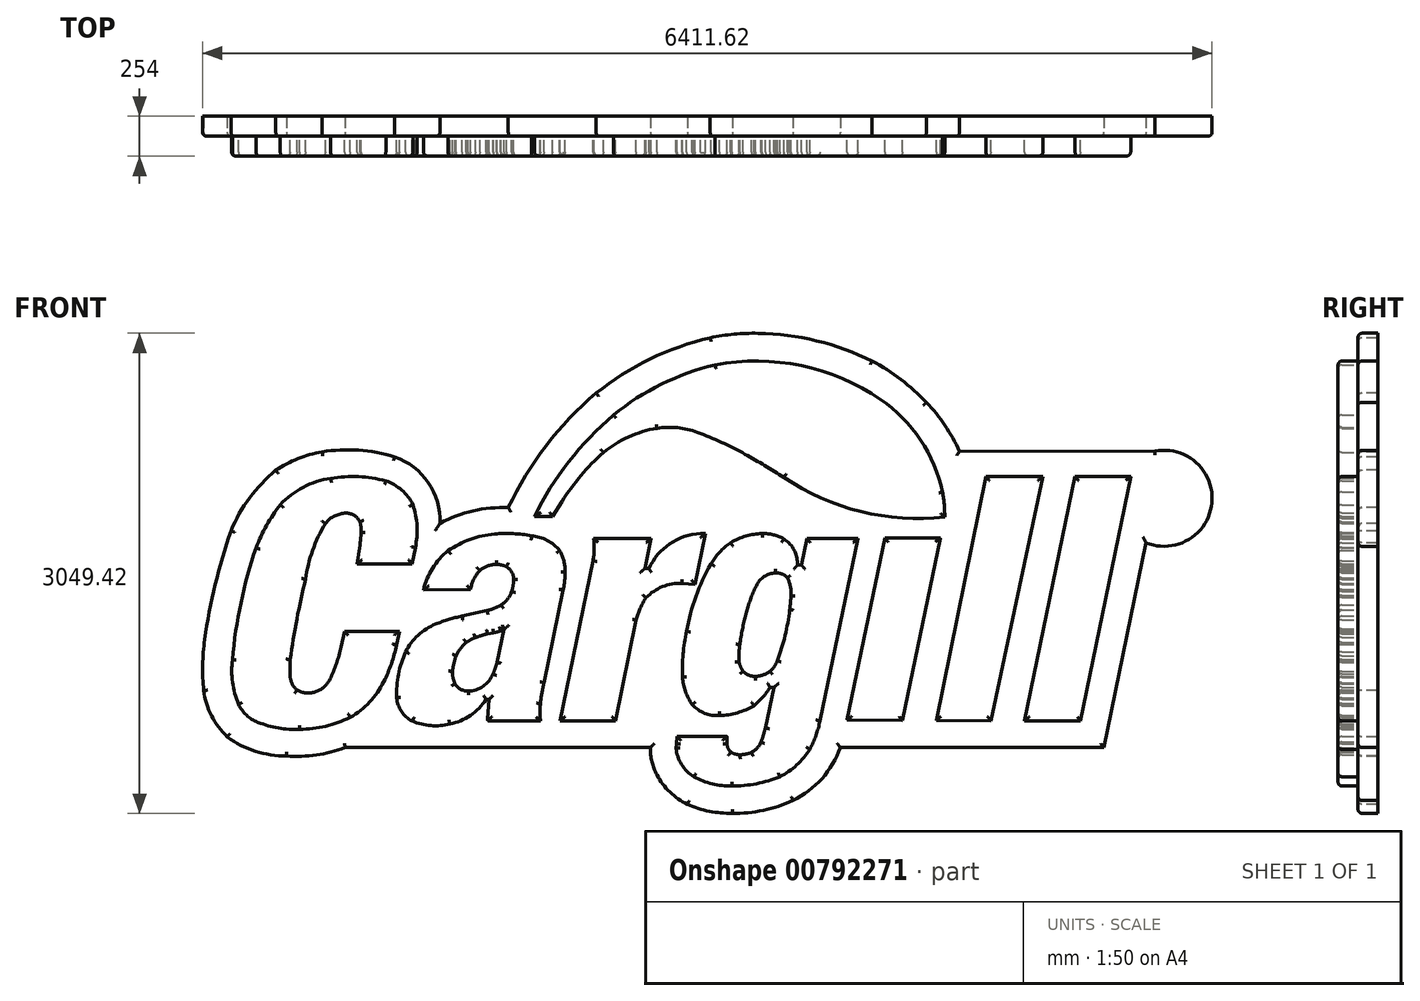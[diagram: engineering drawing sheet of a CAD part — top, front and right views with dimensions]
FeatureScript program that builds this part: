
annotation { "Feature Type Name" : "Feature", "Feature Type Description" : "" }
export const myFeature = defineFeature(function(context is Context, id is Id, definition is map)
    precondition{}
    {
        {
            var Q0;
            Q0=qCreatedBy(makeId("Front.planeOp"),FACE);
            var sketch = newSketch(context, id + "F0", { "sketchPlane" : qUnion([Q0])});
            skArc(sketch, "E0", {"start": v(-1853.74, 164.8) * mm, "mid": v(-1842.63, 301.62) * mm, "end": v(-1868.91, 436.37) * mm});
            skArc(sketch, "E1", {"start": v(-1868.91, 436.37) * mm, "mid": v(-1939.86, 529.44) * mm, "end": v(-2041.08, 588.2) * mm});
            skArc(sketch, "E2", {"start": v(-2041.08, 588.2) * mm, "mid": v(-2215, 614.67) * mm, "end": v(-2390.62, 604.46) * mm});
            skArc(sketch, "E3", {"start": v(-2390.62, 604.46) * mm, "mid": v(-2565.27, 547.67) * mm, "end": v(-2711.35, 436.37) * mm});
            skArc(sketch, "E4", {"start": v(-2711.35, 436.37) * mm, "mid": v(-2798.03, 305.5) * mm, "end": v(-2864.96, 163.5) * mm});
            skArc(sketch, "E5", {"start": v(-2864.96, 163.5) * mm, "mid": v(-2961.53, -187) * mm, "end": v(-3015.73, -546.5) * mm});
            skArc(sketch, "E6", {"start": v(-3015.73, -546.5) * mm, "mid": v(-3014.28, -691.03) * mm, "end": v(-2977.3, -830.75) * mm});
            skArc(sketch, "E7", {"start": v(-2977.3, -830.75) * mm, "mid": v(-2926.34, -899.69) * mm, "end": v(-2853.8, -945.37) * mm});
            skArc(sketch, "E8", {"start": v(-2853.8, -945.37) * mm, "mid": v(-2723.54, -981.4) * mm, "end": v(-2588.63, -989.4) * mm});
            skArc(sketch, "E9", {"start": v(-2588.63, -989.4) * mm, "mid": v(-2423.63, -970.22) * mm, "end": v(-2267.44, -913.67) * mm});
            skArc(sketch, "E10", {"start": v(-2267.44, -913.67) * mm, "mid": v(-2144.2, -816.58) * mm, "end": v(-2054.04, -688.19) * mm});
            skArc(sketch, "E11", {"start": v(-2054.04, -688.19) * mm, "mid": v(-2005.72, -573.66) * mm, "end": v(-1972.93, -453.75) * mm});
            skArc(sketch, "E12", {"start": v(-2395.81, -671.3) * mm, "mid": v(-2354.54, -570.88) * mm, "end": v(-2324.8, -466.47) * mm});
            skArc(sketch, "E13", {"start": v(-2490, -752.83) * mm, "mid": v(-2434.28, -722.02) * mm, "end": v(-2395.81, -671.3) * mm});
            skArc(sketch, "E14", {"start": v(-2605.17, -740.5) * mm, "mid": v(-2548.82, -758.18) * mm, "end": v(-2490, -752.83) * mm});
            skArc(sketch, "E15", {"start": v(-2648.28, -656.13) * mm, "mid": v(-2634.95, -702.52) * mm, "end": v(-2605.17, -740.5) * mm});
            skArc(sketch, "E16", {"start": v(-2648.28, -546.5) * mm, "mid": v(-2650.48, -601.32) * mm, "end": v(-2648.28, -656.13) * mm});
            skArc(sketch, "E17", {"start": v(-2424.98, 317.68) * mm, "mid": v(-2505.79, 147.06) * mm, "end": v(-2550.67, -36.31) * mm});
            skArc(sketch, "E18", {"start": v(-2291.59, 383.09) * mm, "mid": v(-2365.8, 365.72) * mm, "end": v(-2424.98, 317.68) * mm});
            skArc(sketch, "E19", {"start": v(-2205.97, 328.47) * mm, "mid": v(-2240.72, 368.4) * mm, "end": v(-2291.59, 383.09) * mm});
            skArc(sketch, "E20", {"start": v(-2198.16, 261.18) * mm, "mid": v(-2199.1, 295.17) * mm, "end": v(-2205.97, 328.47) * mm});
            skArc(sketch, "E21", {"start": v(-2205.6, 181.3) * mm, "mid": v(-2200.92, 221.14) * mm, "end": v(-2198.16, 261.18) * mm});
            skLineSegment(sketch, "E22", {"start": v(-2205.6, 181.3) * mm, "end": v(-2222.74, 60.72) * mm});
            skLineSegment(sketch, "E23", {"start": v(-2222.74, 60.72) * mm, "end": v(-1875.09, 60.72) * mm});
            skLineSegment(sketch, "E24", {"start": v(-1875.09, 60.72) * mm, "end": v(-1853.74, 164.8) * mm});
            skLineSegment(sketch, "E25", {"start": v(-2324.8, -466.47) * mm, "end": v(-2302.4, -366.84) * mm});
            skLineSegment(sketch, "E26", {"start": v(-2302.4, -366.84) * mm, "end": v(-1954.97, -366.84) * mm});
            skLineSegment(sketch, "E27", {"start": v(-1954.97, -366.84) * mm, "end": v(-1972.93, -453.75) * mm});
            skArc(sketch, "E28", {"start": v(-2550.67, -36.31) * mm, "mid": v(-2606.06, -290.15) * mm, "end": v(-2648.28, -546.5) * mm});
            skLineSegment(sketch, "E29", {"start": v(888.51, -931.26) * mm, "end": v(1128.72, 225.76) * mm});
            skLineSegment(sketch, "E30", {"start": v(1128.72, 225.76) * mm, "end": v(1480.56, 225.76) * mm});
            skLineSegment(sketch, "E31", {"start": v(1480.56, 225.76) * mm, "end": v(1240.36, -934.65) * mm});
            skLineSegment(sketch, "E32", {"start": v(1240.36, -934.65) * mm, "end": v(888.51, -931.26) * mm});
            skLineSegment(sketch, "E33", {"start": v(1454.71, -932.42) * mm, "end": v(1770.63, 615.9) * mm});
            skLineSegment(sketch, "E34", {"start": v(1770.63, 615.9) * mm, "end": v(2132.1, 615.9) * mm});
            skLineSegment(sketch, "E35", {"start": v(2132.1, 615.9) * mm, "end": v(1801.94, -935.26) * mm});
            skLineSegment(sketch, "E36", {"start": v(1801.94, -935.26) * mm, "end": v(1454.71, -932.42) * mm});
            skLineSegment(sketch, "E37", {"start": v(2337.02, 615.9) * mm, "end": v(2015.4, -935.26) * mm});
            skLineSegment(sketch, "E38", {"start": v(2015.4, -935.26) * mm, "end": v(2371.17, -935.26) * mm});
            skLineSegment(sketch, "E39", {"start": v(2371.17, -935.26) * mm, "end": v(2689.94, 615.9) * mm});
            skLineSegment(sketch, "E40", {"start": v(2689.94, 615.9) * mm, "end": v(2337.02, 615.9) * mm});
            skCircle(sketch, "E41", {"center": v(2877.8, 479.28) * mm, "radius": 141.1 * mm});
            skArc(sketch, "E42", {"start": v(-595.08, 1006.86) * mm, "mid": v(-879.13, 709.64) * mm, "end": v(-1098.05, 361.64) * mm});
            skArc(sketch, "E43", {"start": v(50.14, 1325.24) * mm, "mid": v(-290.23, 1202.04) * mm, "end": v(-595.08, 1006.86) * mm});
            skArc(sketch, "E44", {"start": v(1101.08, 1105.47) * mm, "mid": v(597.44, 1319.77) * mm, "end": v(50.14, 1325.24) * mm});
            skArc(sketch, "E45", {"start": v(1495.54, 516.6) * mm, "mid": v(1354.34, 848.57) * mm, "end": v(1101.08, 1105.47) * mm});
            skArc(sketch, "E46", {"start": v(1509.17, 358.66) * mm, "mid": v(1505.54, 437.9) * mm, "end": v(1495.54, 516.6) * mm});
            skArc(sketch, "E47", {"start": v(487.58, 610.95) * mm, "mid": v(975.81, 393.45) * mm, "end": v(1509.17, 358.66) * mm});
            skArc(sketch, "E48", {"start": v(-659.18, 768.54) * mm, "mid": v(-802.03, 621.55) * mm, "end": v(-923.49, 456.45) * mm});
            skArc(sketch, "E49", {"start": v(-318.77, 922.46) * mm, "mid": v(-499.03, 867.74) * mm, "end": v(-659.18, 768.54) * mm});
            skArc(sketch, "E50", {"start": v(-62.13, 896.46) * mm, "mid": v(-188.8, 925.73) * mm, "end": v(-318.77, 922.46) * mm});
            skArc(sketch, "E51", {"start": v(241.27, 757.08) * mm, "mid": v(92.44, 833.01) * mm, "end": v(-62.13, 896.46) * mm});
            skArc(sketch, "E52", {"start": v(487.58, 610.95) * mm, "mid": v(365.23, 685.38) * mm, "end": v(241.27, 757.08) * mm});
            skLineSegment(sketch, "E53", {"start": v(-923.49, 456.45) * mm, "end": v(-983.7, 361.64) * mm});
            skLineSegment(sketch, "E54", {"start": v(-983.7, 361.64) * mm, "end": v(-1098.05, 361.64) * mm});
            skArc(sketch, "E55", {"start": v(2787.2, 194.54) * mm, "mid": v(3205.58, 448.6) * mm, "end": v(2842.16, 776.5) * mm});
            skArc(sketch, "E56", {"start": v(-1645.22, 144.75) * mm, "mid": v(-1743.53, 33.23) * mm, "end": v(-1801.4, -103.72) * mm});
            skArc(sketch, "E57", {"start": v(-1351, 250.45) * mm, "mid": v(-1505.1, 217.08) * mm, "end": v(-1645.22, 144.75) * mm});
            skArc(sketch, "E58", {"start": v(-1114.36, 239.4) * mm, "mid": v(-1232.33, 252.59) * mm, "end": v(-1351, 250.45) * mm});
            skArc(sketch, "E59", {"start": v(-936.89, 144.75) * mm, "mid": v(-1016.16, 209.83) * mm, "end": v(-1114.36, 239.4) * mm});
            skArc(sketch, "E60", {"start": v(-901.92, 8.7) * mm, "mid": v(-909.62, 79.24) * mm, "end": v(-936.89, 144.75) * mm});
            skArc(sketch, "E61", {"start": v(-914.54, -105.31) * mm, "mid": v(-905.3, -48.63) * mm, "end": v(-901.92, 8.7) * mm});
            skArc(sketch, "E62", {"start": v(-1035.83, -693.63) * mm, "mid": v(-1049.72, -759.54) * mm, "end": v(-1058.93, -826.26) * mm});
            skArc(sketch, "E63", {"start": v(-1058.93, -826.26) * mm, "mid": v(-1062.94, -880.8) * mm, "end": v(-1058.93, -935.35) * mm});
            skArc(sketch, "E64", {"start": v(-1634.35, -956.35) * mm, "mid": v(-1503.9, -901.1) * mm, "end": v(-1404.74, -799.92) * mm});
            skArc(sketch, "E65", {"start": v(-1873.12, -938.04) * mm, "mid": v(-1755.2, -966.35) * mm, "end": v(-1634.35, -956.35) * mm});
            skArc(sketch, "E66", {"start": v(-1971.27, -789.36) * mm, "mid": v(-1941.6, -876.52) * mm, "end": v(-1873.12, -938.04) * mm});
            skArc(sketch, "E67", {"start": v(-1915, -497.35) * mm, "mid": v(-1960.34, -640.04) * mm, "end": v(-1971.27, -789.36) * mm});
            skArc(sketch, "E68", {"start": v(-1724.64, -321.62) * mm, "mid": v(-1835.8, -392.18) * mm, "end": v(-1915, -497.35) * mm});
            skArc(sketch, "E69", {"start": v(-1556.88, -270.9) * mm, "mid": v(-1642.04, -292.02) * mm, "end": v(-1724.64, -321.62) * mm});
            skArc(sketch, "E70", {"start": v(-1242.46, -113.42) * mm, "mid": v(-1232.17, -75.81) * mm, "end": v(-1229.71, -36.9) * mm});
            skArc(sketch, "E71", {"start": v(-1229.71, -36.9) * mm, "mid": v(-1241.56, 9.56) * mm, "end": v(-1275.57, 43.36) * mm});
            skArc(sketch, "E72", {"start": v(-1275.57, 43.36) * mm, "mid": v(-1305.97, 54.07) * mm, "end": v(-1338.06, 57.12) * mm});
            skArc(sketch, "E73", {"start": v(-1338.06, 57.12) * mm, "mid": v(-1394.55, 48.2) * mm, "end": v(-1443.54, 18.7) * mm});
            skArc(sketch, "E74", {"start": v(-1443.54, 18.7) * mm, "mid": v(-1482.62, -37.61) * mm, "end": v(-1503.74, -102.83) * mm});
            skLineSegment(sketch, "E75", {"start": v(-1801.4, -103.72) * mm, "end": v(-1503.74, -102.83) * mm});
            skArc(sketch, "E76", {"start": v(-1308.09, -199.85) * mm, "mid": v(-1267.42, -162.6) * mm, "end": v(-1242.46, -113.42) * mm});
            skArc(sketch, "E77", {"start": v(-1398.04, -235.27) * mm, "mid": v(-1351.72, -220.98) * mm, "end": v(-1308.09, -199.85) * mm});
            skLineSegment(sketch, "E78", {"start": v(-1556.88, -270.9) * mm, "end": v(-1398.04, -235.27) * mm});
            skLineSegment(sketch, "E79", {"start": v(-1035.83, -693.63) * mm, "end": v(-914.54, -105.31) * mm});
            skLineSegment(sketch, "E80", {"start": v(-1058.93, -935.35) * mm, "end": v(-1393.05, -935.35) * mm});
            skLineSegment(sketch, "E81", {"start": v(-1393.05, -935.35) * mm, "end": v(-1393.66, -925.25) * mm});
            skLineSegment(sketch, "E82", {"start": v(-1393.66, -925.25) * mm, "end": v(-1385.77, -799.35) * mm});
            skLineSegment(sketch, "E83", {"start": v(-1385.77, -799.35) * mm, "end": v(-1404.74, -799.92) * mm});
            skArc(sketch, "E84", {"start": v(-1517.46, -747.03) * mm, "mid": v(-1422.59, -716.33) * mm, "end": v(-1360.21, -638.53) * mm});
            skArc(sketch, "E85", {"start": v(-1360.21, -638.53) * mm, "mid": v(-1345.94, -601.96) * mm, "end": v(-1334.75, -564.32) * mm});
            skArc(sketch, "E86", {"start": v(-1600.82, -701.27) * mm, "mid": v(-1565.62, -735.95) * mm, "end": v(-1517.46, -747.03) * mm});
            skArc(sketch, "E87", {"start": v(-1617.05, -621.91) * mm, "mid": v(-1614.45, -662.72) * mm, "end": v(-1600.82, -701.27) * mm});
            skArc(sketch, "E88", {"start": v(-1593.8, -522.98) * mm, "mid": v(-1608.96, -571.62) * mm, "end": v(-1617.05, -621.91) * mm});
            skArc(sketch, "E89", {"start": v(-1529.83, -438.31) * mm, "mid": v(-1566.7, -476.96) * mm, "end": v(-1593.8, -522.98) * mm});
            skArc(sketch, "E90", {"start": v(-1472.28, -406.96) * mm, "mid": v(-1501.86, -421.16) * mm, "end": v(-1529.83, -438.31) * mm});
            skArc(sketch, "E91", {"start": v(-1395.4, -384.73) * mm, "mid": v(-1434.41, -393.86) * mm, "end": v(-1472.28, -406.96) * mm});
            skArc(sketch, "E92", {"start": v(-1356.2, -376.5) * mm, "mid": v(-1333.26, -371.34) * mm, "end": v(-1310.69, -364.8) * mm});
            skArc(sketch, "E93", {"start": v(-1310.69, -364.8) * mm, "mid": v(-1300.48, -359.9) * mm, "end": v(-1291.06, -353.65) * mm});
            skLineSegment(sketch, "E94", {"start": v(-1291.06, -353.65) * mm, "end": v(-1289.84, -353.65) * mm});
            skLineSegment(sketch, "E95", {"start": v(-1289.84, -353.65) * mm, "end": v(-1334.75, -564.32) * mm});
            skLineSegment(sketch, "E96", {"start": v(-1395.4, -384.73) * mm, "end": v(-1356.2, -376.5) * mm});
            skArc(sketch, "E97", {"start": v(-387.94, -153.2) * mm, "mid": v(-425.7, -221.92) * mm, "end": v(-450.55, -296.3) * mm});
            skArc(sketch, "E98", {"start": v(-160.28, -62.94) * mm, "mid": v(-283.64, -84.04) * mm, "end": v(-387.94, -153.2) * mm});
            skArc(sketch, "E99", {"start": v(-42.88, 253.05) * mm, "mid": v(-237.67, 187.9) * mm, "end": v(-370.17, 30.95) * mm});
            skArc(sketch, "E100", {"start": v(-724.98, 80.6) * mm, "mid": v(-717.66, 151.06) * mm, "end": v(-720.65, 221.83) * mm});
            skLineSegment(sketch, "E101", {"start": v(-720.65, 221.83) * mm, "end": v(-356.51, 221.83) * mm});
            skLineSegment(sketch, "E102", {"start": v(-356.51, 221.83) * mm, "end": v(-395.89, 30.95) * mm});
            skLineSegment(sketch, "E103", {"start": v(-395.89, 30.95) * mm, "end": v(-370.17, 30.95) * mm});
            skLineSegment(sketch, "E104", {"start": v(-160.28, -62.94) * mm, "end": v(-77.7, -69.74) * mm});
            skLineSegment(sketch, "E105", {"start": v(-77.7, -69.74) * mm, "end": v(-10.97, 253.27) * mm});
            skLineSegment(sketch, "E106", {"start": v(-10.97, 253.27) * mm, "end": v(-42.88, 253.05) * mm});
            skLineSegment(sketch, "E107", {"start": v(-724.98, 80.6) * mm, "end": v(-933.72, -935.84) * mm});
            skLineSegment(sketch, "E108", {"start": v(-933.72, -935.84) * mm, "end": v(-582.85, -935.84) * mm});
            skLineSegment(sketch, "E109", {"start": v(-582.85, -935.84) * mm, "end": v(-450.55, -296.3) * mm});
            skArc(sketch, "E110", {"start": v(-197.36, -1108.56) * mm, "mid": v(-162.64, -1213.34) * mm, "end": v(-84.09, -1290.87) * mm});
            skArc(sketch, "E111", {"start": v(-84.09, -1290.87) * mm, "mid": v(32.73, -1336.3) * mm, "end": v(157.28, -1350.3) * mm});
            skArc(sketch, "E112", {"start": v(157.28, -1350.3) * mm, "mid": v(312.42, -1335.05) * mm, "end": v(461.93, -1290.87) * mm});
            skArc(sketch, "E113", {"start": v(461.93, -1290.87) * mm, "mid": v(568.6, -1216.6) * mm, "end": v(652.22, -1117.08) * mm});
            skArc(sketch, "E114", {"start": v(652.22, -1117.08) * mm, "mid": v(690.73, -1028.55) * mm, "end": v(716.96, -935.64) * mm});
            skArc(sketch, "E115", {"start": v(572.85, 76.64) * mm, "mid": v(546.3, 158.5) * mm, "end": v(486.42, 220.31) * mm});
            skArc(sketch, "E116", {"start": v(486.42, 220.31) * mm, "mid": v(420.25, 246) * mm, "end": v(349.65, 253.33) * mm});
            skArc(sketch, "E117", {"start": v(349.65, 253.33) * mm, "mid": v(245.43, 237.66) * mm, "end": v(148.88, 195.38) * mm});
            skArc(sketch, "E118", {"start": v(148.88, 195.38) * mm, "mid": v(78.8, 134.98) * mm, "end": v(23.09, 61.1) * mm});
            skArc(sketch, "E119", {"start": v(23.09, 61.1) * mm, "mid": v(-71.74, -146.6) * mm, "end": v(-131.48, -366.99) * mm});
            skArc(sketch, "E120", {"start": v(-131.48, -366.99) * mm, "mid": v(-152.88, -512.22) * mm, "end": v(-156.62, -658.97) * mm});
            skArc(sketch, "E121", {"start": v(-156.62, -658.97) * mm, "mid": v(-137.02, -749.7) * mm, "end": v(-95.54, -832.74) * mm});
            skArc(sketch, "E122", {"start": v(-95.54, -832.74) * mm, "mid": v(-16.22, -887.84) * mm, "end": v(79.28, -902.25) * mm});
            skArc(sketch, "E123", {"start": v(79.28, -902.25) * mm, "mid": v(192.1, -884.73) * mm, "end": v(297, -839.73) * mm});
            skArc(sketch, "E124", {"start": v(297, -839.73) * mm, "mid": v(349.1, -791.48) * mm, "end": v(391.28, -734.35) * mm});
            skArc(sketch, "E125", {"start": v(125.8, -1081.2) * mm, "mid": v(132.95, -1110.4) * mm, "end": v(151.27, -1134.24) * mm});
            skArc(sketch, "E126", {"start": v(151.27, -1134.24) * mm, "mid": v(178.83, -1147.69) * mm, "end": v(209.3, -1151.25) * mm});
            skArc(sketch, "E127", {"start": v(209.3, -1151.25) * mm, "mid": v(245.77, -1147.43) * mm, "end": v(280.95, -1137.05) * mm});
            skArc(sketch, "E128", {"start": v(280.95, -1137.05) * mm, "mid": v(317.27, -1109.33) * mm, "end": v(341.79, -1070.79) * mm});
            skArc(sketch, "E129", {"start": v(341.79, -1070.79) * mm, "mid": v(357.27, -1026.34) * mm, "end": v(369.87, -980.98) * mm});
            skArc(sketch, "E130", {"start": v(228.15, -621.33) * mm, "mid": v(263.51, -645.84) * mm, "end": v(305.86, -653.44) * mm});
            skArc(sketch, "E131", {"start": v(305.86, -653.44) * mm, "mid": v(354.88, -644.95) * mm, "end": v(398.92, -621.8) * mm});
            skArc(sketch, "E132", {"start": v(398.92, -621.8) * mm, "mid": v(426.46, -590.15) * mm, "end": v(446.1, -553.08) * mm});
            skArc(sketch, "E133", {"start": v(446.1, -553.08) * mm, "mid": v(495, -394.18) * mm, "end": v(524.3, -230.53) * mm});
            skArc(sketch, "E134", {"start": v(202.74, -560.17) * mm, "mid": v(211.76, -592.28) * mm, "end": v(228.15, -621.33) * mm});
            skArc(sketch, "E135", {"start": v(207.4, -451.93) * mm, "mid": v(202.15, -505.92) * mm, "end": v(202.74, -560.17) * mm});
            skArc(sketch, "E136", {"start": v(246.22, -257.29) * mm, "mid": v(224, -354.05) * mm, "end": v(207.4, -451.93) * mm});
            skArc(sketch, "E137", {"start": v(311.71, -78.12) * mm, "mid": v(274.52, -166.08) * mm, "end": v(246.22, -257.29) * mm});
            skArc(sketch, "E138", {"start": v(434.98, 3.76) * mm, "mid": v(362.16, -20.34) * mm, "end": v(311.71, -78.12) * mm});
            skArc(sketch, "E139", {"start": v(508.94, -27.5) * mm, "mid": v(475.45, -3.61) * mm, "end": v(434.98, 3.76) * mm});
            skArc(sketch, "E140", {"start": v(532.27, -140.63) * mm, "mid": v(528.63, -82.4) * mm, "end": v(508.94, -27.5) * mm});
            skArc(sketch, "E141", {"start": v(524.3, -230.53) * mm, "mid": v(529.17, -185.66) * mm, "end": v(532.27, -140.63) * mm});
            skLineSegment(sketch, "E142", {"start": v(572.85, 76.64) * mm, "end": v(574.8, 53.82) * mm});
            skLineSegment(sketch, "E143", {"start": v(574.8, 53.82) * mm, "end": v(599.34, 53.82) * mm});
            skLineSegment(sketch, "E144", {"start": v(599.34, 53.82) * mm, "end": v(633.67, 221.52) * mm});
            skLineSegment(sketch, "E145", {"start": v(633.67, 221.52) * mm, "end": v(957.92, 221.52) * mm});
            skLineSegment(sketch, "E146", {"start": v(957.92, 221.52) * mm, "end": v(716.96, -935.64) * mm});
            skLineSegment(sketch, "E147", {"start": v(391.28, -734.35) * mm, "end": v(398.54, -722.3) * mm});
            skLineSegment(sketch, "E148", {"start": v(398.54, -722.3) * mm, "end": v(423.93, -722.3) * mm});
            skLineSegment(sketch, "E149", {"start": v(423.93, -722.3) * mm, "end": v(369.87, -980.98) * mm});
            skLineSegment(sketch, "E150", {"start": v(-197.36, -1108.56) * mm, "end": v(-196.23, -1081.82) * mm});
            skLineSegment(sketch, "E151", {"start": v(-196.23, -1081.82) * mm, "end": v(-192.26, -1034.4) * mm});
            skLineSegment(sketch, "E152", {"start": v(-192.26, -1034.4) * mm, "end": v(124.38, -1034.4) * mm});
            skLineSegment(sketch, "E153", {"start": v(124.38, -1034.4) * mm, "end": v(125.8, -1081.2) * mm});
            skSolve(sketch);
        }
        {
            var Q0;
            Q0=qCreatedBy(makeId("Front.planeOp"),FACE);
            var sketch = newSketch(context, id + "F1", { "sketchPlane" : qUnion([Q0])});
            skArc(sketch, "E154", {"start": v(-1263.1, 417.94) * mm, "mid": v(-1486.68, 397.96) * mm, "end": v(-1696.83, 319.05) * mm});
            skArc(sketch, "E155", {"start": v(-705.45, 1145) * mm, "mid": v(-1022.9, 811.1) * mm, "end": v(-1263.1, 417.94) * mm});
            skArc(sketch, "E156", {"start": v(19.36, 1496.66) * mm, "mid": v(-362.89, 1361.73) * mm, "end": v(-705.45, 1145) * mm});
            skArc(sketch, "E157", {"start": v(323.61, 1525.55) * mm, "mid": v(170.65, 1519.88) * mm, "end": v(19.36, 1496.66) * mm});
            skArc(sketch, "E158", {"start": v(1047.44, 1349.26) * mm, "mid": v(695.28, 1477.45) * mm, "end": v(323.61, 1525.55) * mm});
            skArc(sketch, "E159", {"start": v(1393.06, 1086.88) * mm, "mid": v(1230.52, 1231.6) * mm, "end": v(1047.44, 1349.26) * mm});
            skArc(sketch, "E160", {"start": v(1602.18, 775.3) * mm, "mid": v(1510.4, 939.67) * mm, "end": v(1393.06, 1086.88) * mm});
            skArc(sketch, "E161", {"start": v(2787.22, 194.85) * mm, "mid": v(3205.6, 448.92) * mm, "end": v(2842.17, 776.81) * mm});
            skArc(sketch, "E162", {"start": v(545.81, -1441.69) * mm, "mid": v(729.01, -1303.36) * mm, "end": v(845.41, -1105.5) * mm});
            skArc(sketch, "E163", {"start": v(159.26, -1523.46) * mm, "mid": v(357.18, -1504.5) * mm, "end": v(545.81, -1441.69) * mm});
            skArc(sketch, "E164", {"start": v(-125.63, -1466.2) * mm, "mid": v(13.7, -1510.36) * mm, "end": v(159.26, -1523.46) * mm});
            skArc(sketch, "E165", {"start": v(-318.77, -1279.57) * mm, "mid": v(-237.11, -1388.32) * mm, "end": v(-125.63, -1466.2) * mm});
            skArc(sketch, "E166", {"start": v(-361.07, -1105.85) * mm, "mid": v(-350.52, -1195.3) * mm, "end": v(-318.77, -1279.57) * mm});
            skArc(sketch, "E167", {"start": v(-2671.48, -1159.3) * mm, "mid": v(-2482.29, -1153.02) * mm, "end": v(-2298.96, -1105.85) * mm});
            skArc(sketch, "E168", {"start": v(-3048.26, -1038.07) * mm, "mid": v(-2869.55, -1128.76) * mm, "end": v(-2671.48, -1159.3) * mm});
            skArc(sketch, "E169", {"start": v(-3197.9, -743.62) * mm, "mid": v(-3148.06, -903.54) * mm, "end": v(-3048.26, -1038.07) * mm});
            skArc(sketch, "E170", {"start": v(-3191.62, -419.78) * mm, "mid": v(-3204.43, -581.52) * mm, "end": v(-3197.9, -743.62) * mm});
            skArc(sketch, "E171", {"start": v(-3024.7, 270.97) * mm, "mid": v(-3124.61, -70.43) * mm, "end": v(-3191.62, -419.78) * mm});
            skArc(sketch, "E172", {"start": v(-2739.82, 655.81) * mm, "mid": v(-2905.7, 480.74) * mm, "end": v(-3024.7, 270.97) * mm});
            skArc(sketch, "E173", {"start": v(-2446.07, 772.23) * mm, "mid": v(-2598.95, 729.17) * mm, "end": v(-2739.82, 655.81) * mm});
            skArc(sketch, "E174", {"start": v(-1984.47, 741.1) * mm, "mid": v(-2213.5, 782.9) * mm, "end": v(-2446.07, 772.23) * mm});
            skArc(sketch, "E175", {"start": v(-1696.83, 319.05) * mm, "mid": v(-1771.43, 577.25) * mm, "end": v(-1984.47, 741.1) * mm});
            skLineSegment(sketch, "E176", {"start": v(845.41, -1105.5) * mm, "end": v(2520.06, -1105.5) * mm});
            skLineSegment(sketch, "E177", {"start": v(2520.06, -1105.5) * mm, "end": v(2787.22, 194.85) * mm});
            skLineSegment(sketch, "E178", {"start": v(2842.17, 776.81) * mm, "end": v(1602.18, 775.3) * mm});
            skLineSegment(sketch, "E179", {"start": v(-361.07, -1105.85) * mm, "end": v(-2298.96, -1105.85) * mm});
            skSolve(sketch);
        }
        {
            var Q0;
            Q0=makeQuery(id+"F0.imprint","IMPRINT",FACE,{"disambiguationData":[TD([[makeQuery(id+"F0.imprint","IMPRINT",EDGE,{"derivedFrom":sQuery(id+"F0.wireOp",EDGE,"E0")}),1.0]])]});
            var Q1;
            Q1=makeQuery(id+"F0.imprint","IMPRINT",FACE,{"disambiguationData":[TD([[makeQuery(id+"F0.imprint","IMPRINT",EDGE,{"derivedFrom":sQuery(id+"F0.wireOp",EDGE,"E56")}),1.0]])]});
            var Q2;
            Q2=makeQuery(id+"F0.imprint","IMPRINT",FACE,{"disambiguationData":[TD([[makeQuery(id+"F0.imprint","IMPRINT",EDGE,{"derivedFrom":sQuery(id+"F0.wireOp",EDGE,"E97")}),-1.0]])]});
            var Q3;
            Q3=makeQuery(id+"F0.imprint","IMPRINT",FACE,{"disambiguationData":[TD([[makeQuery(id+"F0.imprint","IMPRINT",EDGE,{"derivedFrom":sQuery(id+"F0.wireOp",EDGE,"E110")}),1.0]])]});
            var Q4;
            Q4=makeQuery(id+"F0.imprint","IMPRINT",FACE,{"disambiguationData":[TD([[makeQuery(id+"F0.imprint","IMPRINT",EDGE,{"derivedFrom":sQuery(id+"F0.wireOp",EDGE,"E29")}),-1.0]])]});
            var Q5;
            Q5=makeQuery(id+"F0.imprint","IMPRINT",FACE,{"disambiguationData":[TD([[makeQuery(id+"F0.imprint","IMPRINT",EDGE,{"derivedFrom":sQuery(id+"F0.wireOp",EDGE,"E33")}),-1.0]])]});
            var Q6;
            Q6=makeQuery(id+"F0.imprint","IMPRINT",FACE,{"disambiguationData":[TD([[makeQuery(id+"F0.imprint","IMPRINT",EDGE,{"derivedFrom":sQuery(id+"F0.wireOp",EDGE,"E37")}),1.0]])]});
            var Q7;
            Q7=makeQuery(id+"F0.imprint","IMPRINT",FACE,{"disambiguationData":[TD([[makeQuery(id+"F0.imprint","IMPRINT",EDGE,{"derivedFrom":sQuery(id+"F0.wireOp",EDGE,"E42")}),1.0]])]});
            extrude(context, id + "F2", {"entities" : qUnion([Q0, Q1, Q2, Q3, Q4, Q5, Q6, Q7]), "depth" : 127 * mm, "offsetDistance" : 25.4 * mm});
        }
        {
            var Q0;
            Q0=makeQuery(id+"F1.imprint","IMPRINT",FACE,{"disambiguationData":[TD([[makeQuery(id+"F1.imprint","IMPRINT",EDGE,{"derivedFrom":sQuery(id+"F1.wireOp",EDGE,"E154")}),1.0]])]});
            extrude(context, id + "F3", {"entities" : qUnion([Q0]), "depth" : -127 * mm, "offsetDistance" : 25.4 * mm});
        }
        {
            var Q0;
            Q0=makeQuery(id+"F3.opExtrude","CAP_FACE",FACE,{"disambiguationData":[OSD([sQuery(id+"F1.wireOp",EDGE,"E154"),sQuery(id+"F1.wireOp",EDGE,"E155"),sQuery(id+"F1.wireOp",EDGE,"E156"),sQuery(id+"F1.wireOp",EDGE,"E157"),sQuery(id+"F1.wireOp",EDGE,"E158"),sQuery(id+"F1.wireOp",EDGE,"E159"),sQuery(id+"F1.wireOp",EDGE,"E160"),sQuery(id+"F1.wireOp",EDGE,"E161"),sQuery(id+"F1.wireOp",EDGE,"E162"),sQuery(id+"F1.wireOp",EDGE,"E163"),sQuery(id+"F1.wireOp",EDGE,"E164"),sQuery(id+"F1.wireOp",EDGE,"E165"),sQuery(id+"F1.wireOp",EDGE,"E166"),sQuery(id+"F1.wireOp",EDGE,"E167"),sQuery(id+"F1.wireOp",EDGE,"E168"),sQuery(id+"F1.wireOp",EDGE,"E169"),sQuery(id+"F1.wireOp",EDGE,"E170"),sQuery(id+"F1.wireOp",EDGE,"E171"),sQuery(id+"F1.wireOp",EDGE,"E172"),sQuery(id+"F1.wireOp",EDGE,"E173"),sQuery(id+"F1.wireOp",EDGE,"E174"),sQuery(id+"F1.wireOp",EDGE,"E175"),sQuery(id+"F1.wireOp",EDGE,"E176"),sQuery(id+"F1.wireOp",EDGE,"E177"),sQuery(id+"F1.wireOp",EDGE,"E178"),sQuery(id+"F1.wireOp",EDGE,"E179")])],"isStart":true});
            var Q1;
            Q1=makeQuery(id+"F2.opExtrude","CAP_FACE",FACE,{"disambiguationData":[OSD([sQuery(id+"F0.wireOp",EDGE,"E0"),sQuery(id+"F0.wireOp",EDGE,"E1"),sQuery(id+"F0.wireOp",EDGE,"E2"),sQuery(id+"F0.wireOp",EDGE,"E3"),sQuery(id+"F0.wireOp",EDGE,"E4"),sQuery(id+"F0.wireOp",EDGE,"E5"),sQuery(id+"F0.wireOp",EDGE,"E6"),sQuery(id+"F0.wireOp",EDGE,"E7"),sQuery(id+"F0.wireOp",EDGE,"E8"),sQuery(id+"F0.wireOp",EDGE,"E9"),sQuery(id+"F0.wireOp",EDGE,"E10"),sQuery(id+"F0.wireOp",EDGE,"E11"),sQuery(id+"F0.wireOp",EDGE,"E12"),sQuery(id+"F0.wireOp",EDGE,"E13"),sQuery(id+"F0.wireOp",EDGE,"E14"),sQuery(id+"F0.wireOp",EDGE,"E15"),sQuery(id+"F0.wireOp",EDGE,"E16"),sQuery(id+"F0.wireOp",EDGE,"E17"),sQuery(id+"F0.wireOp",EDGE,"E18"),sQuery(id+"F0.wireOp",EDGE,"E19"),sQuery(id+"F0.wireOp",EDGE,"E20"),sQuery(id+"F0.wireOp",EDGE,"E21"),sQuery(id+"F0.wireOp",EDGE,"E22"),sQuery(id+"F0.wireOp",EDGE,"E23"),sQuery(id+"F0.wireOp",EDGE,"E24"),sQuery(id+"F0.wireOp",EDGE,"E25"),sQuery(id+"F0.wireOp",EDGE,"E26"),sQuery(id+"F0.wireOp",EDGE,"E27"),sQuery(id+"F0.wireOp",EDGE,"E28")])],"isStart":false});
            var Q2;
            Q2=makeQuery(id+"F2.opExtrude","CAP_FACE",FACE,{"disambiguationData":[OSD([sQuery(id+"F0.wireOp",EDGE,"E56"),sQuery(id+"F0.wireOp",EDGE,"E57"),sQuery(id+"F0.wireOp",EDGE,"E58"),sQuery(id+"F0.wireOp",EDGE,"E59"),sQuery(id+"F0.wireOp",EDGE,"E60"),sQuery(id+"F0.wireOp",EDGE,"E61"),sQuery(id+"F0.wireOp",EDGE,"E62"),sQuery(id+"F0.wireOp",EDGE,"E63"),sQuery(id+"F0.wireOp",EDGE,"E64"),sQuery(id+"F0.wireOp",EDGE,"E65"),sQuery(id+"F0.wireOp",EDGE,"E66"),sQuery(id+"F0.wireOp",EDGE,"E67"),sQuery(id+"F0.wireOp",EDGE,"E68"),sQuery(id+"F0.wireOp",EDGE,"E69"),sQuery(id+"F0.wireOp",EDGE,"E70"),sQuery(id+"F0.wireOp",EDGE,"E71"),sQuery(id+"F0.wireOp",EDGE,"E72"),sQuery(id+"F0.wireOp",EDGE,"E73"),sQuery(id+"F0.wireOp",EDGE,"E74"),sQuery(id+"F0.wireOp",EDGE,"E75"),sQuery(id+"F0.wireOp",EDGE,"E76"),sQuery(id+"F0.wireOp",EDGE,"E77"),sQuery(id+"F0.wireOp",EDGE,"E78"),sQuery(id+"F0.wireOp",EDGE,"E79"),sQuery(id+"F0.wireOp",EDGE,"E80"),sQuery(id+"F0.wireOp",EDGE,"E81"),sQuery(id+"F0.wireOp",EDGE,"E82"),sQuery(id+"F0.wireOp",EDGE,"E83"),sQuery(id+"F0.wireOp",EDGE,"E84"),sQuery(id+"F0.wireOp",EDGE,"E85"),sQuery(id+"F0.wireOp",EDGE,"E86"),sQuery(id+"F0.wireOp",EDGE,"E87"),sQuery(id+"F0.wireOp",EDGE,"E88"),sQuery(id+"F0.wireOp",EDGE,"E89"),sQuery(id+"F0.wireOp",EDGE,"E90"),sQuery(id+"F0.wireOp",EDGE,"E91"),sQuery(id+"F0.wireOp",EDGE,"E92"),sQuery(id+"F0.wireOp",EDGE,"E93"),sQuery(id+"F0.wireOp",EDGE,"E94"),sQuery(id+"F0.wireOp",EDGE,"E95"),sQuery(id+"F0.wireOp",EDGE,"E96")])],"isStart":false});
            var Q3;
            Q3=makeQuery(id+"F2.opExtrude","CAP_FACE",FACE,{"disambiguationData":[OSD([sQuery(id+"F0.wireOp",EDGE,"E97"),sQuery(id+"F0.wireOp",EDGE,"E98"),sQuery(id+"F0.wireOp",EDGE,"E99"),sQuery(id+"F0.wireOp",EDGE,"E100"),sQuery(id+"F0.wireOp",EDGE,"E101"),sQuery(id+"F0.wireOp",EDGE,"E102"),sQuery(id+"F0.wireOp",EDGE,"E103"),sQuery(id+"F0.wireOp",EDGE,"E104"),sQuery(id+"F0.wireOp",EDGE,"E105"),sQuery(id+"F0.wireOp",EDGE,"E106"),sQuery(id+"F0.wireOp",EDGE,"E107"),sQuery(id+"F0.wireOp",EDGE,"E108"),sQuery(id+"F0.wireOp",EDGE,"E109")])],"isStart":false});
            var Q4;
            Q4=makeQuery(id+"F2.opExtrude","CAP_FACE",FACE,{"disambiguationData":[OSD([sQuery(id+"F0.wireOp",EDGE,"E110"),sQuery(id+"F0.wireOp",EDGE,"E111"),sQuery(id+"F0.wireOp",EDGE,"E112"),sQuery(id+"F0.wireOp",EDGE,"E113"),sQuery(id+"F0.wireOp",EDGE,"E114"),sQuery(id+"F0.wireOp",EDGE,"E115"),sQuery(id+"F0.wireOp",EDGE,"E116"),sQuery(id+"F0.wireOp",EDGE,"E117"),sQuery(id+"F0.wireOp",EDGE,"E118"),sQuery(id+"F0.wireOp",EDGE,"E119"),sQuery(id+"F0.wireOp",EDGE,"E120"),sQuery(id+"F0.wireOp",EDGE,"E121"),sQuery(id+"F0.wireOp",EDGE,"E122"),sQuery(id+"F0.wireOp",EDGE,"E123"),sQuery(id+"F0.wireOp",EDGE,"E124"),sQuery(id+"F0.wireOp",EDGE,"E125"),sQuery(id+"F0.wireOp",EDGE,"E126"),sQuery(id+"F0.wireOp",EDGE,"E127"),sQuery(id+"F0.wireOp",EDGE,"E128"),sQuery(id+"F0.wireOp",EDGE,"E129"),sQuery(id+"F0.wireOp",EDGE,"E130"),sQuery(id+"F0.wireOp",EDGE,"E131"),sQuery(id+"F0.wireOp",EDGE,"E132"),sQuery(id+"F0.wireOp",EDGE,"E133"),sQuery(id+"F0.wireOp",EDGE,"E134"),sQuery(id+"F0.wireOp",EDGE,"E135"),sQuery(id+"F0.wireOp",EDGE,"E136"),sQuery(id+"F0.wireOp",EDGE,"E137"),sQuery(id+"F0.wireOp",EDGE,"E138"),sQuery(id+"F0.wireOp",EDGE,"E139"),sQuery(id+"F0.wireOp",EDGE,"E140"),sQuery(id+"F0.wireOp",EDGE,"E141"),sQuery(id+"F0.wireOp",EDGE,"E142"),sQuery(id+"F0.wireOp",EDGE,"E143"),sQuery(id+"F0.wireOp",EDGE,"E144"),sQuery(id+"F0.wireOp",EDGE,"E145"),sQuery(id+"F0.wireOp",EDGE,"E146"),sQuery(id+"F0.wireOp",EDGE,"E147"),sQuery(id+"F0.wireOp",EDGE,"E148"),sQuery(id+"F0.wireOp",EDGE,"E149"),sQuery(id+"F0.wireOp",EDGE,"E150"),sQuery(id+"F0.wireOp",EDGE,"E151"),sQuery(id+"F0.wireOp",EDGE,"E152"),sQuery(id+"F0.wireOp",EDGE,"E153")])],"isStart":false});
            var Q5;
            Q5=makeQuery(id+"F2.opExtrude","CAP_FACE",FACE,{"disambiguationData":[OSD([sQuery(id+"F0.wireOp",EDGE,"E29"),sQuery(id+"F0.wireOp",EDGE,"E30"),sQuery(id+"F0.wireOp",EDGE,"E31"),sQuery(id+"F0.wireOp",EDGE,"E32")])],"isStart":false});
            var Q6;
            Q6=makeQuery(id+"F2.opExtrude","CAP_FACE",FACE,{"disambiguationData":[OSD([sQuery(id+"F0.wireOp",EDGE,"E33"),sQuery(id+"F0.wireOp",EDGE,"E34"),sQuery(id+"F0.wireOp",EDGE,"E35"),sQuery(id+"F0.wireOp",EDGE,"E36")])],"isStart":false});
            var Q7;
            Q7=makeQuery(id+"F2.opExtrude","CAP_FACE",FACE,{"disambiguationData":[OSD([sQuery(id+"F0.wireOp",EDGE,"E37"),sQuery(id+"F0.wireOp",EDGE,"E38"),sQuery(id+"F0.wireOp",EDGE,"E39"),sQuery(id+"F0.wireOp",EDGE,"E40")])],"isStart":false});
            var Q8;
            Q8=makeQuery(id+"F2.opExtrude","CAP_FACE",FACE,{"disambiguationData":[OSD([sQuery(id+"F0.wireOp",EDGE,"E42"),sQuery(id+"F0.wireOp",EDGE,"E43"),sQuery(id+"F0.wireOp",EDGE,"E44"),sQuery(id+"F0.wireOp",EDGE,"E45"),sQuery(id+"F0.wireOp",EDGE,"E46"),sQuery(id+"F0.wireOp",EDGE,"E47"),sQuery(id+"F0.wireOp",EDGE,"E48"),sQuery(id+"F0.wireOp",EDGE,"E49"),sQuery(id+"F0.wireOp",EDGE,"E50"),sQuery(id+"F0.wireOp",EDGE,"E51"),sQuery(id+"F0.wireOp",EDGE,"E52"),sQuery(id+"F0.wireOp",EDGE,"E53"),sQuery(id+"F0.wireOp",EDGE,"E54")])],"isStart":false});
            fillet(context, id + "F4", {"entities" : qUnion([Q0, Q1, Q2, Q3, Q4, Q5, Q6, Q7, Q8]), "radius" : 25.4 * mm, "tangentPropagation" : true, "allowEdgeOverflow" : false});
        }
    });
